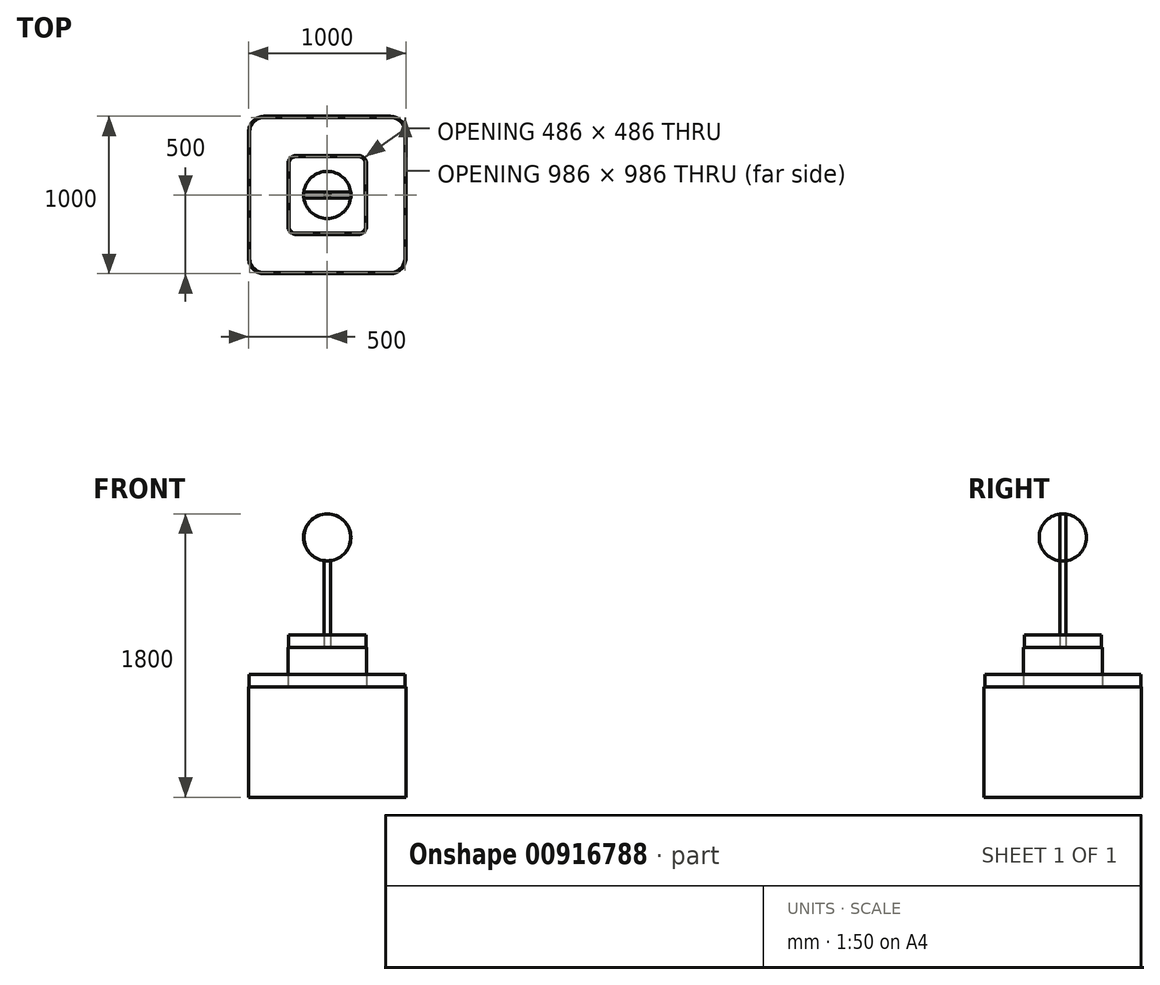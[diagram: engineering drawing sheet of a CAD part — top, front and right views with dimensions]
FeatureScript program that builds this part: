
annotation { "Feature Type Name" : "Feature", "Feature Type Description" : "" }
export const myFeature = defineFeature(function(context is Context, id is Id, definition is map)
    precondition{}
    {
        {
            var Q0;
            Q0=qCreatedBy(makeId("Front.planeOp"),FACE);
            var sketch = newSketch(context, id + "F0", { "sketchPlane" : qUnion([Q0])});
            skLineSegment(sketch, "E0.bottom", {"start": v(-500, 0) * mm, "end": v(500, 0) * mm});
            skLineSegment(sketch, "E0.top", {"start": v(-500, 1500) * mm, "end": v(500, 1500) * mm});
            skLineSegment(sketch, "E0.left", {"start": v(-500, 0) * mm, "end": v(-500, 1500) * mm});
            skLineSegment(sketch, "E0.right", {"start": v(500, 0) * mm, "end": v(500, 1500) * mm});
            skLineSegment(sketch, "E1", {"start": v(-500, 150) * mm, "end": v(500, 150) * mm});
            skLineSegment(sketch, "E2", {"start": v(-500, 700) * mm, "end": v(500, 700) * mm});
            skLineSegment(sketch, "E3", {"start": v(-500, 1470) * mm, "end": v(500, 1470) * mm});
            skLineSegment(sketch, "E4", {"start": v(-500, 1040) * mm, "end": v(500, 1040) * mm});
            skLineSegment(sketch, "E5", {"start": v(-500, 1070) * mm, "end": v(500, 1070) * mm});
            skLineSegment(sketch, "E6.bottom", {"start": v(250, 700) * mm, "end": v(-250, 700) * mm});
            skLineSegment(sketch, "E6.top", {"start": v(250, 1030) * mm, "end": v(-250, 1030) * mm});
            skLineSegment(sketch, "E6.left", {"start": v(250, 700) * mm, "end": v(250, 1030) * mm});
            skLineSegment(sketch, "E6.right", {"start": v(-250, 700) * mm, "end": v(-250, 1030) * mm});
            skPoint(sketch, "E6.middle", {"position": v(0, 865) * mm});
            skLineSegment(sketch, "E7", {"start": v(0, 0) * mm, "end": v(0, 1500) * mm, "construction": true});
            skLineSegment(sketch, "E8.bottom", {"start": v(-25, 1500) * mm, "end": v(25, 1500) * mm});
            skLineSegment(sketch, "E8.top", {"start": v(-25, 700) * mm, "end": v(25, 700) * mm});
            skLineSegment(sketch, "E8.left", {"start": v(-25, 1500) * mm, "end": v(-25, 700) * mm});
            skLineSegment(sketch, "E8.right", {"start": v(25, 1500) * mm, "end": v(25, 700) * mm});
            skPoint(sketch, "E8.middle", {"position": v(0, 1100) * mm});
            skCircle(sketch, "E9", {"center": v(0, 1650) * mm, "radius": 150 * mm});
            skLineSegment(sketch, "E10", {"start": v(0, 1650) * mm, "end": v(0, 1500) * mm, "construction": true});
            skSolve(sketch);
        }
        {
            var Q0;
            Q0=qCreatedBy(makeId("Top.planeOp"),FACE);
            var sketch = newSketch(context, id + "F1", { "sketchPlane" : qUnion([Q0])});
            skLineSegment(sketch, "E11.bottom", {"start": v(500, 500) * mm, "end": v(-500, 500) * mm});
            skLineSegment(sketch, "E11.top", {"start": v(500, -500) * mm, "end": v(-500, -500) * mm});
            skLineSegment(sketch, "E11.left", {"start": v(500, 500) * mm, "end": v(500, -500) * mm});
            skLineSegment(sketch, "E11.right", {"start": v(-500, 500) * mm, "end": v(-500, -500) * mm});
            skPoint(sketch, "E11.middle", {"position": v(0, 0) * mm});
            skLineSegment(sketch, "E12.0", {"start": v(450, 450) * mm, "end": v(-450, 450) * mm});
            skLineSegment(sketch, "E12.1", {"start": v(450, 450) * mm, "end": v(450, -450) * mm});
            skLineSegment(sketch, "E12.2", {"start": v(450, -450) * mm, "end": v(-450, -450) * mm});
            skLineSegment(sketch, "E12.3", {"start": v(-450, 450) * mm, "end": v(-450, -450) * mm});
            skLineSegment(sketch, "E13.bottom", {"start": v(250, 250) * mm, "end": v(-250, 250) * mm});
            skLineSegment(sketch, "E13.top", {"start": v(250, -250) * mm, "end": v(-250, -250) * mm});
            skLineSegment(sketch, "E13.left", {"start": v(250, 250) * mm, "end": v(250, -250) * mm});
            skLineSegment(sketch, "E13.right", {"start": v(-250, 250) * mm, "end": v(-250, -250) * mm});
            skSolve(sketch);
        }
        {
            var Q0;
            Q0=qCreatedBy(makeId("Top.planeOp"),FACE);
            var sketch = newSketch(context, id + "F2", { "sketchPlane" : qUnion([Q0])});
            skLineSegment(sketch, "E14.0", {"start": v(450, 450) * mm, "end": v(-450, 450) * mm});
            skLineSegment(sketch, "E14.1", {"start": v(-450, 450) * mm, "end": v(-450, -450) * mm});
            skLineSegment(sketch, "E14.2", {"start": v(450, -450) * mm, "end": v(-450, -450) * mm});
            skLineSegment(sketch, "E14.3", {"start": v(450, 450) * mm, "end": v(450, -450) * mm});
            skSolve(sketch);
        }
        {
            var Q0;
            Q0=qSketchRegion(id+"F2",true);
            var Q1;
            Q1=sQuery(id+"F0.wireOp",VERTEX,"E1.end");
            extrude(context, id + "F3", {"entities" : qUnion([Q0]), "endBound" : BoundingType.UP_TO_VERTEX, "depth" : 25 * mm, "endBoundEntityVertex" : qUnion([Q1]), "offsetDistance" : 25 * mm});
        }
        {
            var Q0;
            Q0=makeQuery(id+"F3.opExtrude","CAP_FACE",FACE,{"disambiguationData":[OSD([sQuery(id+"F2.wireOp",EDGE,"E14.0"),sQuery(id+"F2.wireOp",EDGE,"E14.1"),sQuery(id+"F2.wireOp",EDGE,"E14.2"),sQuery(id+"F2.wireOp",EDGE,"E14.3")])],"isStart":false});
            var sketch = newSketch(context, id + "F4", { "sketchPlane" : qUnion([Q0])});
            skLineSegment(sketch, "E15.0", {"start": v(500, 500) * mm, "end": v(-500, 500) * mm});
            skLineSegment(sketch, "E15.1", {"start": v(-500, 500) * mm, "end": v(-500, -500) * mm});
            skLineSegment(sketch, "E15.2", {"start": v(500, -500) * mm, "end": v(-500, -500) * mm});
            skLineSegment(sketch, "E15.3", {"start": v(500, 500) * mm, "end": v(500, -500) * mm});
            skSolve(sketch);
        }
        {
            var Q0;
            Q0=qSketchRegion(id+"F4",true);
            var Q1;
            Q1=sQuery(id+"F0.wireOp",VERTEX,"E2.end");
            extrude(context, id + "F5", {"entities" : qUnion([Q0]), "operationType" : NewBodyOperationType.ADD, "endBound" : BoundingType.UP_TO_VERTEX, "depth" : 25 * mm, "endBoundEntityVertex" : qUnion([Q1]), "offsetDistance" : 25 * mm});
        }
        {
            var Q0;
            Q0=makeQuery(id+"F5.opExtrude","CAP_FACE",FACE,{"disambiguationData":[OSD([sQuery(id+"F4.wireOp",EDGE,"E15.0"),sQuery(id+"F4.wireOp",EDGE,"E15.1"),sQuery(id+"F4.wireOp",EDGE,"E15.2"),sQuery(id+"F4.wireOp",EDGE,"E15.3")])],"isStart":false});
            var sketch = newSketch(context, id + "F6", { "sketchPlane" : qUnion([Q0])});
            skLineSegment(sketch, "E16.0", {"start": v(250, 250) * mm, "end": v(-250, 250) * mm});
            skLineSegment(sketch, "E16.1", {"start": v(-250, 250) * mm, "end": v(-250, -250) * mm});
            skLineSegment(sketch, "E16.2", {"start": v(250, 250) * mm, "end": v(250, -250) * mm});
            skLineSegment(sketch, "E16.3", {"start": v(250, -250) * mm, "end": v(-250, -250) * mm});
            skSolve(sketch);
        }
        {
            var Q0;
            Q0 = qSketchRegion(id + "F6", true);
            var Q1;
            Q1=sQuery(id+"F0.wireOp",VERTEX,"E6.top.end");
            extrude(context, id + "F7", {"entities" : qUnion([Q0]), "operationType" : NewBodyOperationType.ADD, "depth" : 250 * mm, "endBoundEntityVertex" : qUnion([Q1]), "offsetDistance" : 25 * mm});
        }
        {
            var Q0;
            Q0=makeQuery(id+"F5.opExtrude","SWEPT_EDGE",EDGE,{"disambiguationData":[OSD([sQuery(id+"F4.wireOp",EDGE,"E15.2"),sQuery(id+"F4.wireOp",EDGE,"E15.3")])]});
            var Q1;
            Q1=makeQuery(id+"F5.opExtrude","SWEPT_EDGE",EDGE,{"disambiguationData":[OSD([sQuery(id+"F4.wireOp",EDGE,"E15.1"),sQuery(id+"F4.wireOp",EDGE,"E15.2")])]});
            var Q2;
            Q2=makeQuery(id+"F5.opExtrude","SWEPT_EDGE",EDGE,{"disambiguationData":[OSD([sQuery(id+"F4.wireOp",EDGE,"E15.0"),sQuery(id+"F4.wireOp",EDGE,"E15.3")])]});
            var Q3;
            Q3=makeQuery(id+"F5.opExtrude","SWEPT_EDGE",EDGE,{"disambiguationData":[OSD([sQuery(id+"F4.wireOp",EDGE,"E15.0"),sQuery(id+"F4.wireOp",EDGE,"E15.1")])]});
            fillet(context, id + "F8", {"entities" : qUnion([Q0, Q1, Q2, Q3]), "radius" : 100 * mm, "tangentPropagation" : true, "allowEdgeOverflow" : false});
        }
        {
            var Q0;
            Q0=makeQuery(id+"F3.opExtrude","SWEPT_EDGE",EDGE,{"disambiguationData":[OSD([sQuery(id+"F2.wireOp",EDGE,"E14.0"),sQuery(id+"F2.wireOp",EDGE,"E14.1")])]});
            var Q1;
            Q1=makeQuery(id+"F3.opExtrude","SWEPT_EDGE",EDGE,{"disambiguationData":[OSD([sQuery(id+"F2.wireOp",EDGE,"E14.1"),sQuery(id+"F2.wireOp",EDGE,"E14.2")])]});
            var Q2;
            Q2=makeQuery(id+"F3.opExtrude","SWEPT_EDGE",EDGE,{"disambiguationData":[OSD([sQuery(id+"F2.wireOp",EDGE,"E14.2"),sQuery(id+"F2.wireOp",EDGE,"E14.3")])]});
            var Q3;
            Q3=makeQuery(id+"F3.opExtrude","SWEPT_EDGE",EDGE,{"disambiguationData":[OSD([sQuery(id+"F2.wireOp",EDGE,"E14.0"),sQuery(id+"F2.wireOp",EDGE,"E14.3")])]});
            fillet(context, id + "F9", {"entities" : qUnion([Q0, Q1, Q2, Q3]), "radius" : 85 * mm, "tangentPropagation" : true, "allowEdgeOverflow" : false});
        }
        {
            var Q0;
            Q0=makeQuery(id+"F7.opExtrude","SWEPT_EDGE",EDGE,{"disambiguationData":[OSD([sQuery(id+"F6.wireOp",EDGE,"E16.1"),sQuery(id+"F6.wireOp",EDGE,"E16.3")])]});
            var Q1;
            Q1=makeQuery(id+"F7.opExtrude","SWEPT_EDGE",EDGE,{"disambiguationData":[OSD([sQuery(id+"F6.wireOp",EDGE,"E16.2"),sQuery(id+"F6.wireOp",EDGE,"E16.3")])]});
            var Q2;
            Q2=makeQuery(id+"F7.opExtrude","SWEPT_EDGE",EDGE,{"disambiguationData":[OSD([sQuery(id+"F6.wireOp",EDGE,"E16.0"),sQuery(id+"F6.wireOp",EDGE,"E16.2")])]});
            var Q3;
            Q3=makeQuery(id+"F7.opExtrude","SWEPT_EDGE",EDGE,{"disambiguationData":[OSD([sQuery(id+"F6.wireOp",EDGE,"E16.0"),sQuery(id+"F6.wireOp",EDGE,"E16.1")])]});
            fillet(context, id + "F10", {"entities" : qUnion([Q0, Q1, Q2, Q3]), "radius" : 50 * mm, "tangentPropagation" : true, "allowEdgeOverflow" : false});
        }
        {
            var Q0;
            {var subQ0=sQuery(id+"F4.wireOp",EDGE,"E15.3");var subQ1=sQuery(id+"F4.wireOp",EDGE,"E15.2");var subQ2=sQuery(id+"F4.wireOp",EDGE,"E15.1");Q0=makeQuery(id+"FzUorhP62OtQi9f_1.boolean.opBoolean","SPLIT",FACE,{"disambiguationData":[TD([makeQuery(id+"F5.opExtrude","SWEPT_FACE",FACE,{"disambiguationData":[OSD([subQ1])]})])],"derivedFrom":makeQuery(id+"F5.opExtrude","CAP_FACE",FACE,{"disambiguationData":[OSD([sQuery(id+"F4.wireOp",EDGE,"E15.0"),subQ2,subQ1,subQ0])],"isStart":false})});}
            var sketch = newSketch(context, id + "F11", { "sketchPlane" : qUnion([Q0])});
            skArc(sketch, "E17.0", {"start": v(-495, 400) * mm, "mid": v(-467.18, 467.18) * mm, "end": v(-400, 495) * mm});
            skLineSegment(sketch, "E17.1", {"start": v(400, 495) * mm, "end": v(-400, 495) * mm});
            skLineSegment(sketch, "E17.2", {"start": v(-495, 400) * mm, "end": v(-495, -400) * mm});
            skArc(sketch, "E17.3", {"start": v(400, 495) * mm, "mid": v(467.18, 467.18) * mm, "end": v(495, 400) * mm});
            skArc(sketch, "E17.4", {"start": v(-400, -495) * mm, "mid": v(-467.18, -467.18) * mm, "end": v(-495, -400) * mm});
            skLineSegment(sketch, "E17.5", {"start": v(400, -495) * mm, "end": v(-400, -495) * mm});
            skArc(sketch, "E17.6", {"start": v(495, -400) * mm, "mid": v(467.18, -467.18) * mm, "end": v(400, -495) * mm});
            skLineSegment(sketch, "E17.7", {"start": v(495, 400) * mm, "end": v(495, -400) * mm});
            skLineSegment(sketch, "E18.0", {"start": v(400, -493) * mm, "end": v(-400, -493) * mm});
            skArc(sketch, "E18.1", {"start": v(493, -400) * mm, "mid": v(465.76, -465.76) * mm, "end": v(400, -493) * mm});
            skArc(sketch, "E18.2", {"start": v(-400, -493) * mm, "mid": v(-465.76, -465.76) * mm, "end": v(-493, -400) * mm});
            skLineSegment(sketch, "E18.3", {"start": v(493, 400) * mm, "end": v(493, -400) * mm});
            skLineSegment(sketch, "E18.4", {"start": v(-493, 400) * mm, "end": v(-493, -400) * mm});
            skArc(sketch, "E18.5", {"start": v(-493, 400) * mm, "mid": v(-465.76, 465.76) * mm, "end": v(-400, 493) * mm});
            skLineSegment(sketch, "E18.6", {"start": v(400, 493) * mm, "end": v(-400, 493) * mm});
            skArc(sketch, "E18.7", {"start": v(400, 493) * mm, "mid": v(465.76, 465.76) * mm, "end": v(493, 400) * mm});
            skSolve(sketch);
        }
        {
            var Q0;
            Q0=qSketchRegion(id+"F11",true);
            extrude(context, id + "F12", {"entities" : qUnion([Q0]), "depth" : 80 * mm, "offsetDistance" : 25 * mm});
        }
        {
            var Q0;
            Q0=makeQuery(id+"F7.opExtrude","CAP_FACE",FACE,{"disambiguationData":[OSD([sQuery(id+"F6.wireOp",EDGE,"E16.0"),sQuery(id+"F6.wireOp",EDGE,"E16.1"),sQuery(id+"F6.wireOp",EDGE,"E16.2"),sQuery(id+"F6.wireOp",EDGE,"E16.3")])],"isStart":false});
            var sketch = newSketch(context, id + "F13", { "sketchPlane" : qUnion([Q0])});
            skLineSegment(sketch, "E19.0", {"start": v(200, 245) * mm, "end": v(-200, 245) * mm});
            skArc(sketch, "E19.1", {"start": v(242, 203) * mm, "mid": v(229.7, 232.7) * mm, "end": v(200, 245) * mm});
            skArc(sketch, "E19.2", {"start": v(-200, 245) * mm, "mid": v(-231.82, 231.82) * mm, "end": v(-245, 200) * mm});
            skLineSegment(sketch, "E19.3", {"start": v(242, 203) * mm, "end": v(245, -199.34) * mm});
            skLineSegment(sketch, "E19.4", {"start": v(-245, 200) * mm, "end": v(-245, -200) * mm});
            skArc(sketch, "E19.5", {"start": v(-245, -200) * mm, "mid": v(-231.82, -231.82) * mm, "end": v(-200, -245) * mm});
            skLineSegment(sketch, "E19.6", {"start": v(200, -245) * mm, "end": v(-200, -245) * mm});
            skArc(sketch, "E19.7", {"start": v(200, -245) * mm, "mid": v(232.05, -231.58) * mm, "end": v(245, -199.34) * mm});
            skArc(sketch, "E20.0", {"start": v(-200, 243) * mm, "mid": v(-230.4, 230.4) * mm, "end": v(-243, 200) * mm});
            skLineSegment(sketch, "E20.1", {"start": v(200, 243) * mm, "end": v(-200, 243) * mm});
            skLineSegment(sketch, "E20.2", {"start": v(-243, 200) * mm, "end": v(-243, -200) * mm});
            skArc(sketch, "E20.3", {"start": v(240, 203) * mm, "mid": v(228.28, 231.28) * mm, "end": v(200, 243) * mm});
            skArc(sketch, "E20.4", {"start": v(-243, -200) * mm, "mid": v(-230.4, -230.4) * mm, "end": v(-200, -243) * mm});
            skLineSegment(sketch, "E20.5", {"start": v(200, -243) * mm, "end": v(-200, -243) * mm});
            skArc(sketch, "E20.6", {"start": v(200, -243) * mm, "mid": v(230.4, -230.4) * mm, "end": v(243, -200) * mm});
            skLineSegment(sketch, "E20.7", {"start": v(240, 203) * mm, "end": v(243, -200) * mm});
            skSolve(sketch);
        }
        {
            var Q0;
            Q0 = qSketchRegion(id + "F13", true);
            extrude(context, id + "F14", {"entities" : qUnion([Q0]), "depth" : 80 * mm, "offsetDistance" : 25 * mm});
        }
        {
            var Q0;
            Q0=qCreatedBy(makeId("Top.planeOp"),FACE);
            var sketch = newSketch(context, id + "F15", { "sketchPlane" : qUnion([Q0])});
            skCircle(sketch, "E21", {"center": v(0, 0) * mm, "radius": 20 * mm});
            skSolve(sketch);
        }
        {
            var Q0;
            Q0 = qSketchRegion(id + "F15", true);
            extrude(context, id + "F16", {"entities" : qUnion([Q0]), "operationType" : NewBodyOperationType.ADD, "depth" : 1600 * mm, "offsetDistance" : 25 * mm});
        }
        {
            var Q0;
            Q0=qCreatedBy(makeId("Front.planeOp"),FACE);
            var sketch = newSketch(context, id + "F17", { "sketchPlane" : qUnion([Q0])});
            skArc(sketch, "E22.0", {"start": v(0, 1500) * mm, "mid": v(150, 1650) * mm, "end": v(0, 1800) * mm});
            skLineSegment(sketch, "E23", {"start": v(0, 1500) * mm, "end": v(0, 1800) * mm});
            skSolve(sketch);
        }
        {
            var Q0;
            Q0=qCreatedBy(makeId("Front.planeOp"),FACE);
            var sketch = newSketch(context, id + "F18", { "sketchPlane" : qUnion([Q0])});
            skCircle(sketch, "E24.0", {"center": v(0, 1650) * mm, "radius": 150 * mm});
            skSolve(sketch);
        }
        {
            var Q0;
            Q0 = qSketchRegion(id + "F18", true);
            extrude(context, id + "F19", {"entities" : qUnion([Q0]), "operationType" : NewBodyOperationType.ADD, "endBound" : BoundingType.SYMMETRIC, "depth" : 40 * mm, "offsetDistance" : 25 * mm});
        }
        {
            var Q0;
            Q0=makeQuery(id+"F5.opExtrude","CAP_FACE",FACE,{"disambiguationData":[OSD([sQuery(id+"F4.wireOp",EDGE,"E15.0"),sQuery(id+"F4.wireOp",EDGE,"E15.1"),sQuery(id+"F4.wireOp",EDGE,"E15.2"),sQuery(id+"F4.wireOp",EDGE,"E15.3")])],"isStart":true});
            var sketch = newSketch(context, id + "F20", { "sketchPlane" : qUnion([Q0])});
            skArc(sketch, "E25.0", {"start": v(-400, 500) * mm, "mid": v(-470.71, 470.71) * mm, "end": v(-500, 400) * mm});
            skLineSegment(sketch, "E25.1", {"start": v(-500, -400) * mm, "end": v(-500, 400) * mm});
            skLineSegment(sketch, "E25.2", {"start": v(400, 500) * mm, "end": v(-400, 500) * mm});
            skLineSegment(sketch, "E25.3", {"start": v(500, -400) * mm, "end": v(500, 400) * mm});
            skArc(sketch, "E25.4", {"start": v(500, 400) * mm, "mid": v(470.71, 470.71) * mm, "end": v(400, 500) * mm});
            skArc(sketch, "E25.5", {"start": v(400, -500) * mm, "mid": v(470.71, -470.71) * mm, "end": v(500, -400) * mm});
            skLineSegment(sketch, "E25.6", {"start": v(400, -500) * mm, "end": v(-400, -500) * mm});
            skPoint(sketch, "E25.7", {"position": v(470.71, 470.71) * mm});
            skPoint(sketch, "E25.8", {"position": v(470.71, -470.71) * mm});
            skPoint(sketch, "E25.9", {"position": v(-470.71, -470.71) * mm});
            skSolve(sketch);
        }
        {
            var Q0;
            Q0=makeQuery(id+"F20.imprint","IMPRINT",FACE,{"disambiguationData":[TD([[makeQuery(id+"F20.imprint","IMPRINT",EDGE,{"derivedFrom":sQuery(id+"F20.wireOp",EDGE,"E25.0")}),1.0]])]});
            var Q1;
            Q1=makeQuery(id+"F3.opExtrude","CAP_FACE",FACE,{"disambiguationData":[OSD([sQuery(id+"F2.wireOp",EDGE,"E14.0"),sQuery(id+"F2.wireOp",EDGE,"E14.1"),sQuery(id+"F2.wireOp",EDGE,"E14.2"),sQuery(id+"F2.wireOp",EDGE,"E14.3")])],"isStart":true});
            extrude(context, id + "F21", {"entities" : qUnion([Q0]), "operationType" : NewBodyOperationType.ADD, "endBound" : BoundingType.UP_TO_SURFACE, "depth" : 25 * mm, "endBoundEntityFace" : qUnion([Q1]), "offsetDistance" : 25 * mm});
        }
        {
            var Q0;
            Q0 = qSketchRegion(id + "F17", true);
            var Q1;
            Q1=sQuery(id+"F17.wireOp",EDGE,"E23");
            revolve(context, id + "F22", {"operationType" : NewBodyOperationType.ADD, "surfaceOperationType" : NewSurfaceOperationType.NEW, "entities" : qUnion([Q0]), "axis" : qUnion([Q1]), "revolveType" : RevolveType.FULL});
        }
    });
